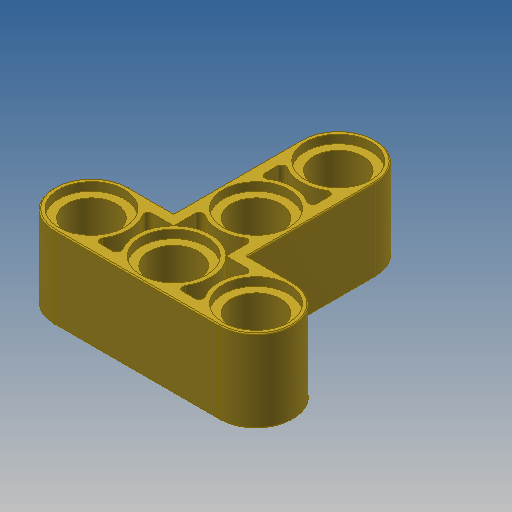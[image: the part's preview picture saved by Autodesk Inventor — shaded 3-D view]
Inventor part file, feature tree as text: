
AUTODESK INVENTOR PART (.ipt)
format: ipt  version: 2022.2 (Build 262287000, 287)  size: 316,416 bytes
history: native  units: mm
features: extrude x3, mirror x1, fillet x1
ambient origin geometry x8: Origin, YZ Plane, XZ Plane, XY Plane, X Axis, Y Axis, Z Axis, Center Point
bodies: Solid1 (feature_tree)
feature tree (5):
  extrude  "Extrusion1"  Depth=4.8mm
  extrude  "Extrusion7"  Depth=6.4mm
  extrude  "Extrusion8"  Depth=8.0mm TaperAngle=0.0deg
  mirror  "Mirror1"
  fillet  "Fillet1"  Radius=7.2mm
